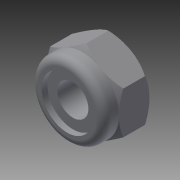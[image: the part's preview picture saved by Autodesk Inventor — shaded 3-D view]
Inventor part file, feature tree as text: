
AUTODESK INVENTOR PART (.ipt)
format: ipt  version: 2015 SP1 (Build 190203100, 203)  size: 150,528 bytes
history: native  units: in
note: dims shown in document units (in); Inventor stores cm internally (conversion verified against a paired STEP export)
features: fillet x1, other x1, imported_body x1
ambient origin geometry x8: Origin, YZ Plane, XZ Plane, XY Plane, X Axis, Y Axis, Z Axis, Center Point
bodies: Body1 (feature_tree)
feature tree (3):
  fillet  "Fillet1"  [1 undecoded]
  other  "#10 LockNut.ipt1"
  imported_body  "Base1"
note: 1 required parameter value undecoded (feature->parameter linkage not recoverable at this tier; creation-order binding heuristic only, values carry confidence <= 0.55)
